# Revit family: 873-00-001-DN1800
name_source: partatom
category: Pipe Accessories
units: mm (PartAtom-declared; Revit-internal decimal feet)

## family parameters
Always vertical = Yes
Cut with Voids When Loaded = No
Part Type = Valve - Breaks Into
Round Connector Dimension = Use Diameter
Shared = No
Work Plane-Based = No

## types (2) — shared parameters
873-1800-00-041000 = DN1800_PN10
873-1800-00-141000 = DN1800_PN16
A = 400 mm  [stored 1.31234 ft]
Angle = 22.50°
Body_Wallthicknss = 10 mm  [stored 0.0328084 ft]
DN = 1800 mm  [stored 5.90551 ft]
Description_ = AVK DISMANTLING JOINT
Flange_thickness = 20 mm  [stored 0.0656168 ft]
Id(Radius) = 900 mm  [stored 2.95276 ft]
Search_table = 873-00-001-DN1800
URL product pages = https://www.avkvalves.com
d1 = 2020 mm  [stored 6.6273 ft]

## per-type parameters (varying)
| type | L | T | d2 |
| DN1800_PN10 | 640 mm  [stored 2.09974 ft] | 45 mm  [stored 0.147638 ft] | 1058 mm |
| DN1800_PN16 | 730 mm  [stored 2.39501 ft] | 52 mm | 1065 mm  [stored 3.49409 ft] |

note: [stored X ft] marks values corroborated as IEEE doubles in the binary element streams (Revit-internal decimal feet)

## geometry (parser evidence)
native form markers: Sweep x3
no freeform markers — native parametric forms only
